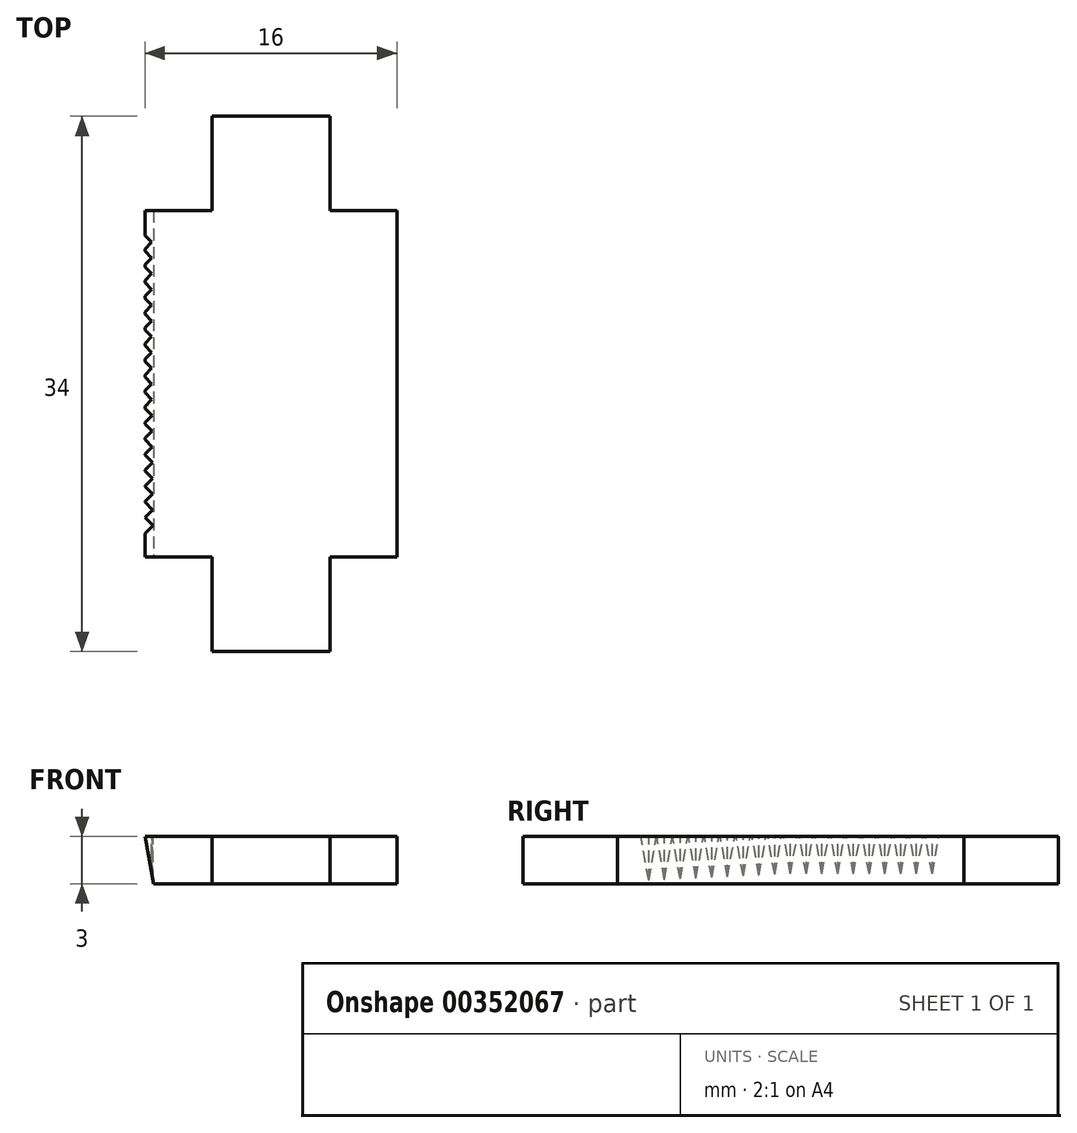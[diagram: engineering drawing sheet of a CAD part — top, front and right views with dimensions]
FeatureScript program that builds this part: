
annotation { "Feature Type Name" : "Feature", "Feature Type Description" : "" }
export const myFeature = defineFeature(function(context is Context, id is Id, definition is map)
    precondition{}
    {
        {
            var Q0;
            Q0=qCreatedBy(makeId("Front.planeOp"),FACE);
            var sketch = newSketch(context, id + "F0", { "sketchPlane" : qUnion([Q0])});
            skLineSegment(sketch, "E0.bottom", {"start": v(8, -1.5) * mm, "end": v(-8, -1.5) * mm});
            skLineSegment(sketch, "E0.top", {"start": v(8, 1.5) * mm, "end": v(-8, 1.5) * mm});
            skLineSegment(sketch, "E0.left", {"start": v(8, -1.5) * mm, "end": v(8, 1.5) * mm});
            skLineSegment(sketch, "E0.right", {"start": v(-8, -1.5) * mm, "end": v(-8, 1.5) * mm});
            skPoint(sketch, "E0.middle", {"position": v(0, 0) * mm});
            skSolve(sketch);
        }
        {
            var Q0;
            Q0=makeQuery(id+"F0.imprint","IMPRINT",FACE,{"disambiguationData":[TD([[makeQuery(id+"F0.imprint","IMPRINT",EDGE,{"derivedFrom":sQuery(id+"F0.wireOp",EDGE,"E0.bottom")}),-1.0]])]});
            extrude(context, id + "F1", {"entities" : qUnion([Q0]), "depth" : 22 * mm});
        }
        {
            var Q0;
            Q0=makeQuery(id+"F1.opExtrude","CAP_FACE",FACE,{"disambiguationData":[OSD([sQuery(id+"F0.wireOp",EDGE,"E0.bottom"),sQuery(id+"F0.wireOp",EDGE,"E0.top"),sQuery(id+"F0.wireOp",EDGE,"E0.left"),sQuery(id+"F0.wireOp",EDGE,"E0.right")])],"isStart":false});
            var sketch = newSketch(context, id + "F2", { "sketchPlane" : qUnion([Q0])});
            skLineSegment(sketch, "E1.bottom", {"start": v(3.75, -1.5) * mm, "end": v(-3.75, -1.5) * mm});
            skLineSegment(sketch, "E1.top", {"start": v(3.75, 1.5) * mm, "end": v(-3.75, 1.5) * mm});
            skLineSegment(sketch, "E1.left", {"start": v(3.75, -1.5) * mm, "end": v(3.75, 1.5) * mm});
            skLineSegment(sketch, "E1.right", {"start": v(-3.75, -1.5) * mm, "end": v(-3.75, 1.5) * mm});
            skPoint(sketch, "E1.middle", {"position": v(0, 0) * mm});
            skSolve(sketch);
        }
        {
            var Q0;
            Q0=makeQuery(id+"F2.imprint","IMPRINT",FACE,{"disambiguationData":[TD([[makeQuery(id+"F2.imprint","IMPRINT",EDGE,{"derivedFrom":sQuery(id+"F2.wireOp",EDGE,"E1.bottom")}),-1.0]])]});
            extrude(context, id + "F3", {"entities" : qUnion([Q0]), "operationType" : NewBodyOperationType.ADD, "depth" : 6 * mm});
        }
        {
            var Q0;
            Q0=makeQuery(id+"F1.opExtrude","CAP_FACE",FACE,{"disambiguationData":[OSD([sQuery(id+"F0.wireOp",EDGE,"E0.bottom"),sQuery(id+"F0.wireOp",EDGE,"E0.top"),sQuery(id+"F0.wireOp",EDGE,"E0.left"),sQuery(id+"F0.wireOp",EDGE,"E0.right")])],"isStart":true});
            var sketch = newSketch(context, id + "F4", { "sketchPlane" : qUnion([Q0])});
            skLineSegment(sketch, "E2.bottom", {"start": v(-3.75, -1.5) * mm, "end": v(3.75, -1.5) * mm});
            skLineSegment(sketch, "E2.top", {"start": v(-3.75, 1.5) * mm, "end": v(3.75, 1.5) * mm});
            skLineSegment(sketch, "E2.left", {"start": v(-3.75, -1.5) * mm, "end": v(-3.75, 1.5) * mm});
            skLineSegment(sketch, "E2.right", {"start": v(3.75, -1.5) * mm, "end": v(3.75, 1.5) * mm});
            skPoint(sketch, "E2.middle", {"position": v(0, 0) * mm});
            skSolve(sketch);
        }
        {
            var Q0;
            Q0=makeQuery(id+"F4.imprint","IMPRINT",FACE,{"disambiguationData":[TD([[makeQuery(id+"F4.imprint","IMPRINT",EDGE,{"derivedFrom":sQuery(id+"F4.wireOp",EDGE,"E2.bottom")}),1.0]])]});
            extrude(context, id + "F5", {"entities" : qUnion([Q0]), "operationType" : NewBodyOperationType.ADD, "depth" : 6 * mm});
        }
        {
            var Q0;
            Q0=makeQuery(id+"F5.boolean.opBoolean","MERGE",FACE,{"derivedFrom":[makeQuery(id+"F3.boolean.opBoolean","MERGE",FACE,{"derivedFrom":[makeQuery(id+"F1.opExtrude","SWEPT_FACE",FACE,{"disambiguationData":[OSD([sQuery(id+"F0.wireOp",EDGE,"E0.top")])]}),makeQuery(id+"F3.opExtrude","SWEPT_FACE",FACE,{"disambiguationData":[OSD([sQuery(id+"F2.wireOp",EDGE,"E1.top")])]})]}),makeQuery(id+"F5.opExtrude","SWEPT_FACE",FACE,{"disambiguationData":[OSD([sQuery(id+"F4.wireOp",EDGE,"E2.top")])]})]});
            var sketch = newSketch(context, id + "F6", { "sketchPlane" : qUnion([Q0])});
            skLineSegment(sketch, "E3", {"start": v(-8, -11) * mm, "end": v(8, -11) * mm, "construction": true});
            skLineSegment(sketch, "E4", {"start": v(-7.5, -11) * mm, "end": v(-8, -10.5) * mm});
            skLineSegment(sketch, "E5", {"start": v(-7.5, -11) * mm, "end": v(-8, -11.5) * mm});
            skPoint(sketch, "E6.orphan", {"position": v(-8.5, -10) * mm});
            skPoint(sketch, "E7.0.1.0", {"position": v(-8.5, -11) * mm});
            skLineSegment(sketch, "E7.0.1.1", {"start": v(-7.5, -12) * mm, "end": v(-8, -12.5) * mm});
            skLineSegment(sketch, "E7.0.1.2", {"start": v(-7.5, -12) * mm, "end": v(-8, -11.5) * mm});
            skPoint(sketch, "E7.0.2.0", {"position": v(-8.5, -12) * mm});
            skLineSegment(sketch, "E7.0.2.1", {"start": v(-7.5, -13) * mm, "end": v(-8, -13.5) * mm});
            skLineSegment(sketch, "E7.0.2.2", {"start": v(-7.5, -13) * mm, "end": v(-8, -12.5) * mm});
            skPoint(sketch, "E7.0.3.0", {"position": v(-8.5, -13) * mm});
            skLineSegment(sketch, "E7.0.3.1", {"start": v(-7.5, -14) * mm, "end": v(-8, -14.5) * mm});
            skLineSegment(sketch, "E7.0.3.2", {"start": v(-7.5, -14) * mm, "end": v(-8, -13.5) * mm});
            skPoint(sketch, "E7.0.4.0", {"position": v(-8.5, -14) * mm});
            skLineSegment(sketch, "E7.0.4.1", {"start": v(-7.5, -15) * mm, "end": v(-8, -15.5) * mm});
            skLineSegment(sketch, "E7.0.4.2", {"start": v(-7.5, -15) * mm, "end": v(-8, -14.5) * mm});
            skPoint(sketch, "E7.0.5.0", {"position": v(-8.5, -15) * mm});
            skLineSegment(sketch, "E7.0.5.1", {"start": v(-7.5, -16) * mm, "end": v(-8, -16.5) * mm});
            skLineSegment(sketch, "E7.0.5.2", {"start": v(-7.5, -16) * mm, "end": v(-8, -15.5) * mm});
            skPoint(sketch, "E7.0.6.0", {"position": v(-8.5, -16) * mm});
            skLineSegment(sketch, "E7.0.6.1", {"start": v(-7.5, -17) * mm, "end": v(-8, -17.5) * mm});
            skLineSegment(sketch, "E7.0.6.2", {"start": v(-7.5, -17) * mm, "end": v(-8, -16.5) * mm});
            skPoint(sketch, "E7.0.7.0", {"position": v(-8.5, -17) * mm});
            skLineSegment(sketch, "E7.0.7.1", {"start": v(-7.5, -18) * mm, "end": v(-8, -18.5) * mm});
            skLineSegment(sketch, "E7.0.7.2", {"start": v(-7.5, -18) * mm, "end": v(-8, -17.5) * mm});
            skPoint(sketch, "E7.0.8.0", {"position": v(-8.5, -18) * mm});
            skLineSegment(sketch, "E7.0.8.1", {"start": v(-7.5, -19) * mm, "end": v(-8, -19.5) * mm});
            skLineSegment(sketch, "E7.0.8.2", {"start": v(-7.5, -19) * mm, "end": v(-8, -18.5) * mm});
            skPoint(sketch, "E7.0.9.0", {"position": v(-8.5, -19) * mm});
            skLineSegment(sketch, "E7.0.9.1", {"start": v(-7.5, -20) * mm, "end": v(-8, -20.5) * mm});
            skLineSegment(sketch, "E7.0.9.2", {"start": v(-7.5, -20) * mm, "end": v(-8, -19.5) * mm});
            skPoint(sketch, "E7.1.0.0", {"position": v(-8.5, -9) * mm});
            skLineSegment(sketch, "E7.1.0.1", {"start": v(-7.5, -10) * mm, "end": v(-8, -10.5) * mm});
            skLineSegment(sketch, "E7.1.0.2", {"start": v(-7.5, -10) * mm, "end": v(-8, -9.5) * mm});
            skPoint(sketch, "E7.1.2.0", {"position": v(-8.5, -11) * mm});
            skLineSegment(sketch, "E7.1.2.1", {"start": v(-7.5, -12) * mm, "end": v(-8, -12.5) * mm});
            skLineSegment(sketch, "E7.1.2.2", {"start": v(-7.5, -12) * mm, "end": v(-8, -11.5) * mm});
            skPoint(sketch, "E7.1.3.0", {"position": v(-8.5, -12) * mm});
            skLineSegment(sketch, "E7.1.3.1", {"start": v(-7.5, -13) * mm, "end": v(-8, -13.5) * mm});
            skLineSegment(sketch, "E7.1.3.2", {"start": v(-7.5, -13) * mm, "end": v(-8, -12.5) * mm});
            skPoint(sketch, "E7.1.4.0", {"position": v(-8.5, -13) * mm});
            skLineSegment(sketch, "E7.1.4.1", {"start": v(-7.5, -14) * mm, "end": v(-8, -14.5) * mm});
            skLineSegment(sketch, "E7.1.4.2", {"start": v(-7.5, -14) * mm, "end": v(-8, -13.5) * mm});
            skPoint(sketch, "E7.1.5.0", {"position": v(-8.5, -14) * mm});
            skLineSegment(sketch, "E7.1.5.1", {"start": v(-7.5, -15) * mm, "end": v(-8, -15.5) * mm});
            skLineSegment(sketch, "E7.1.5.2", {"start": v(-7.5, -15) * mm, "end": v(-8, -14.5) * mm});
            skPoint(sketch, "E7.1.6.0", {"position": v(-8.5, -15) * mm});
            skLineSegment(sketch, "E7.1.6.1", {"start": v(-7.5, -16) * mm, "end": v(-8, -16.5) * mm});
            skLineSegment(sketch, "E7.1.6.2", {"start": v(-7.5, -16) * mm, "end": v(-8, -15.5) * mm});
            skPoint(sketch, "E7.1.7.0", {"position": v(-8.5, -16) * mm});
            skLineSegment(sketch, "E7.1.7.1", {"start": v(-7.5, -17) * mm, "end": v(-8, -17.5) * mm});
            skLineSegment(sketch, "E7.1.7.2", {"start": v(-7.5, -17) * mm, "end": v(-8, -16.5) * mm});
            skPoint(sketch, "E7.1.8.0", {"position": v(-8.5, -17) * mm});
            skLineSegment(sketch, "E7.1.8.1", {"start": v(-7.5, -18) * mm, "end": v(-8, -18.5) * mm});
            skLineSegment(sketch, "E7.1.8.2", {"start": v(-7.5, -18) * mm, "end": v(-8, -17.5) * mm});
            skPoint(sketch, "E7.1.9.0", {"position": v(-8.5, -18) * mm});
            skLineSegment(sketch, "E7.1.9.1", {"start": v(-7.5, -19) * mm, "end": v(-8, -19.5) * mm});
            skLineSegment(sketch, "E7.1.9.2", {"start": v(-7.5, -19) * mm, "end": v(-8, -18.5) * mm});
            skPoint(sketch, "E7.2.0.0", {"position": v(-8.52, -8) * mm});
            skLineSegment(sketch, "E7.2.0.1", {"start": v(-7.52, -9) * mm, "end": v(-8.02, -9.5) * mm});
            skLineSegment(sketch, "E7.2.0.2", {"start": v(-7.52, -9) * mm, "end": v(-8.02, -8.5) * mm});
            skPoint(sketch, "E7.2.1.0", {"position": v(-8.52, -9) * mm});
            skLineSegment(sketch, "E7.2.1.1", {"start": v(-7.52, -10) * mm, "end": v(-8.02, -10.5) * mm});
            skLineSegment(sketch, "E7.2.1.2", {"start": v(-7.52, -10) * mm, "end": v(-8.02, -9.5) * mm});
            skPoint(sketch, "E7.2.2.0", {"position": v(-8.52, -10) * mm});
            skLineSegment(sketch, "E7.2.2.1", {"start": v(-7.52, -11) * mm, "end": v(-8.02, -11.5) * mm});
            skLineSegment(sketch, "E7.2.2.2", {"start": v(-7.52, -11) * mm, "end": v(-8.02, -10.5) * mm});
            skPoint(sketch, "E7.2.3.0", {"position": v(-8.52, -11) * mm});
            skLineSegment(sketch, "E7.2.3.1", {"start": v(-7.52, -12) * mm, "end": v(-8.02, -12.5) * mm});
            skLineSegment(sketch, "E7.2.3.2", {"start": v(-7.52, -12) * mm, "end": v(-8.02, -11.5) * mm});
            skPoint(sketch, "E7.2.4.0", {"position": v(-8.52, -12) * mm});
            skLineSegment(sketch, "E7.2.4.1", {"start": v(-7.52, -13) * mm, "end": v(-8.02, -13.5) * mm});
            skLineSegment(sketch, "E7.2.4.2", {"start": v(-7.52, -13) * mm, "end": v(-8.02, -12.5) * mm});
            skPoint(sketch, "E7.2.5.0", {"position": v(-8.52, -13) * mm});
            skLineSegment(sketch, "E7.2.5.1", {"start": v(-7.52, -14) * mm, "end": v(-8.02, -14.5) * mm});
            skLineSegment(sketch, "E7.2.5.2", {"start": v(-7.52, -14) * mm, "end": v(-8.02, -13.5) * mm});
            skPoint(sketch, "E7.2.6.0", {"position": v(-8.52, -14) * mm});
            skLineSegment(sketch, "E7.2.6.1", {"start": v(-7.52, -15) * mm, "end": v(-8.02, -15.5) * mm});
            skLineSegment(sketch, "E7.2.6.2", {"start": v(-7.52, -15) * mm, "end": v(-8.02, -14.5) * mm});
            skPoint(sketch, "E7.2.7.0", {"position": v(-8.52, -15) * mm});
            skLineSegment(sketch, "E7.2.7.1", {"start": v(-7.52, -16) * mm, "end": v(-8.02, -16.5) * mm});
            skLineSegment(sketch, "E7.2.7.2", {"start": v(-7.52, -16) * mm, "end": v(-8.02, -15.5) * mm});
            skPoint(sketch, "E7.2.8.0", {"position": v(-8.52, -16) * mm});
            skLineSegment(sketch, "E7.2.8.1", {"start": v(-7.52, -17) * mm, "end": v(-8.02, -17.5) * mm});
            skLineSegment(sketch, "E7.2.8.2", {"start": v(-7.52, -17) * mm, "end": v(-8.02, -16.5) * mm});
            skPoint(sketch, "E7.2.9.0", {"position": v(-8.52, -17) * mm});
            skLineSegment(sketch, "E7.2.9.1", {"start": v(-7.52, -18) * mm, "end": v(-8.02, -18.5) * mm});
            skLineSegment(sketch, "E7.2.9.2", {"start": v(-7.52, -18) * mm, "end": v(-8.02, -17.5) * mm});
            skPoint(sketch, "E7.3.0.0", {"position": v(-8.52, -7) * mm});
            skLineSegment(sketch, "E7.3.0.1", {"start": v(-7.52, -8) * mm, "end": v(-8.02, -8.5) * mm});
            skLineSegment(sketch, "E7.3.0.2", {"start": v(-7.52, -8) * mm, "end": v(-8.02, -7.5) * mm});
            skPoint(sketch, "E7.3.1.0", {"position": v(-8.52, -8) * mm});
            skLineSegment(sketch, "E7.3.1.1", {"start": v(-7.52, -9) * mm, "end": v(-8.02, -9.5) * mm});
            skLineSegment(sketch, "E7.3.1.2", {"start": v(-7.52, -9) * mm, "end": v(-8.02, -8.5) * mm});
            skPoint(sketch, "E7.3.2.0", {"position": v(-8.52, -9) * mm});
            skLineSegment(sketch, "E7.3.2.1", {"start": v(-7.52, -10) * mm, "end": v(-8.02, -10.5) * mm});
            skLineSegment(sketch, "E7.3.2.2", {"start": v(-7.52, -10) * mm, "end": v(-8.02, -9.5) * mm});
            skPoint(sketch, "E7.3.3.0", {"position": v(-8.52, -10) * mm});
            skLineSegment(sketch, "E7.3.3.1", {"start": v(-7.52, -11) * mm, "end": v(-8.02, -11.5) * mm});
            skLineSegment(sketch, "E7.3.3.2", {"start": v(-7.52, -11) * mm, "end": v(-8.02, -10.5) * mm});
            skPoint(sketch, "E7.3.4.0", {"position": v(-8.52, -11) * mm});
            skLineSegment(sketch, "E7.3.4.1", {"start": v(-7.52, -12) * mm, "end": v(-8.02, -12.5) * mm});
            skLineSegment(sketch, "E7.3.4.2", {"start": v(-7.52, -12) * mm, "end": v(-8.02, -11.5) * mm});
            skPoint(sketch, "E7.3.5.0", {"position": v(-8.52, -12) * mm});
            skLineSegment(sketch, "E7.3.5.1", {"start": v(-7.52, -13) * mm, "end": v(-8.02, -13.5) * mm});
            skLineSegment(sketch, "E7.3.5.2", {"start": v(-7.52, -13) * mm, "end": v(-8.02, -12.5) * mm});
            skPoint(sketch, "E7.3.6.0", {"position": v(-8.52, -13) * mm});
            skLineSegment(sketch, "E7.3.6.1", {"start": v(-7.52, -14) * mm, "end": v(-8.02, -14.5) * mm});
            skLineSegment(sketch, "E7.3.6.2", {"start": v(-7.52, -14) * mm, "end": v(-8.02, -13.5) * mm});
            skPoint(sketch, "E7.3.7.0", {"position": v(-8.52, -14) * mm});
            skLineSegment(sketch, "E7.3.7.1", {"start": v(-7.52, -15) * mm, "end": v(-8.02, -15.5) * mm});
            skLineSegment(sketch, "E7.3.7.2", {"start": v(-7.52, -15) * mm, "end": v(-8.02, -14.5) * mm});
            skPoint(sketch, "E7.3.8.0", {"position": v(-8.52, -15) * mm});
            skLineSegment(sketch, "E7.3.8.1", {"start": v(-7.52, -16) * mm, "end": v(-8.02, -16.5) * mm});
            skLineSegment(sketch, "E7.3.8.2", {"start": v(-7.52, -16) * mm, "end": v(-8.02, -15.5) * mm});
            skPoint(sketch, "E7.3.9.0", {"position": v(-8.52, -16) * mm});
            skLineSegment(sketch, "E7.3.9.1", {"start": v(-7.52, -17) * mm, "end": v(-8.02, -17.5) * mm});
            skLineSegment(sketch, "E7.3.9.2", {"start": v(-7.52, -17) * mm, "end": v(-8.02, -16.5) * mm});
            skPoint(sketch, "E7.4.0.0", {"position": v(-8.53, -6) * mm});
            skLineSegment(sketch, "E7.4.0.1", {"start": v(-7.53, -7) * mm, "end": v(-8.03, -7.5) * mm});
            skLineSegment(sketch, "E7.4.0.2", {"start": v(-7.53, -7) * mm, "end": v(-8.03, -6.5) * mm});
            skPoint(sketch, "E7.4.1.0", {"position": v(-8.53, -7) * mm});
            skLineSegment(sketch, "E7.4.1.1", {"start": v(-7.53, -8) * mm, "end": v(-8.03, -8.5) * mm});
            skLineSegment(sketch, "E7.4.1.2", {"start": v(-7.53, -8) * mm, "end": v(-8.03, -7.5) * mm});
            skPoint(sketch, "E7.4.2.0", {"position": v(-8.53, -8) * mm});
            skLineSegment(sketch, "E7.4.2.1", {"start": v(-7.53, -9) * mm, "end": v(-8.03, -9.5) * mm});
            skLineSegment(sketch, "E7.4.2.2", {"start": v(-7.53, -9) * mm, "end": v(-8.03, -8.5) * mm});
            skPoint(sketch, "E7.4.3.0", {"position": v(-8.53, -9) * mm});
            skLineSegment(sketch, "E7.4.3.1", {"start": v(-7.53, -10) * mm, "end": v(-8.03, -10.5) * mm});
            skLineSegment(sketch, "E7.4.3.2", {"start": v(-7.53, -10) * mm, "end": v(-8.03, -9.5) * mm});
            skPoint(sketch, "E7.4.4.0", {"position": v(-8.53, -10) * mm});
            skLineSegment(sketch, "E7.4.4.1", {"start": v(-7.53, -11) * mm, "end": v(-8.03, -11.5) * mm});
            skLineSegment(sketch, "E7.4.4.2", {"start": v(-7.53, -11) * mm, "end": v(-8.03, -10.5) * mm});
            skPoint(sketch, "E7.4.5.0", {"position": v(-8.53, -11) * mm});
            skLineSegment(sketch, "E7.4.5.1", {"start": v(-7.53, -12) * mm, "end": v(-8.03, -12.5) * mm});
            skLineSegment(sketch, "E7.4.5.2", {"start": v(-7.53, -12) * mm, "end": v(-8.03, -11.5) * mm});
            skPoint(sketch, "E7.4.6.0", {"position": v(-8.53, -12) * mm});
            skLineSegment(sketch, "E7.4.6.1", {"start": v(-7.53, -13) * mm, "end": v(-8.03, -13.5) * mm});
            skLineSegment(sketch, "E7.4.6.2", {"start": v(-7.53, -13) * mm, "end": v(-8.03, -12.5) * mm});
            skPoint(sketch, "E7.4.7.0", {"position": v(-8.53, -13) * mm});
            skLineSegment(sketch, "E7.4.7.1", {"start": v(-7.53, -14) * mm, "end": v(-8.03, -14.5) * mm});
            skLineSegment(sketch, "E7.4.7.2", {"start": v(-7.53, -14) * mm, "end": v(-8.03, -13.5) * mm});
            skPoint(sketch, "E7.4.8.0", {"position": v(-8.53, -14) * mm});
            skLineSegment(sketch, "E7.4.8.1", {"start": v(-7.53, -15) * mm, "end": v(-8.03, -15.5) * mm});
            skLineSegment(sketch, "E7.4.8.2", {"start": v(-7.53, -15) * mm, "end": v(-8.03, -14.5) * mm});
            skPoint(sketch, "E7.4.9.0", {"position": v(-8.53, -15) * mm});
            skLineSegment(sketch, "E7.4.9.1", {"start": v(-7.53, -16) * mm, "end": v(-8.03, -16.5) * mm});
            skLineSegment(sketch, "E7.4.9.2", {"start": v(-7.53, -16) * mm, "end": v(-8.03, -15.5) * mm});
            skPoint(sketch, "E7.5.0.0", {"position": v(-8.54, -5) * mm});
            skLineSegment(sketch, "E7.5.0.1", {"start": v(-7.54, -6) * mm, "end": v(-8.04, -6.5) * mm});
            skLineSegment(sketch, "E7.5.0.2", {"start": v(-7.54, -6) * mm, "end": v(-8.04, -5.5) * mm});
            skPoint(sketch, "E7.5.1.0", {"position": v(-8.54, -6) * mm});
            skLineSegment(sketch, "E7.5.1.1", {"start": v(-7.54, -7) * mm, "end": v(-8.04, -7.5) * mm});
            skLineSegment(sketch, "E7.5.1.2", {"start": v(-7.54, -7) * mm, "end": v(-8.04, -6.5) * mm});
            skPoint(sketch, "E7.5.2.0", {"position": v(-8.54, -7) * mm});
            skLineSegment(sketch, "E7.5.2.1", {"start": v(-7.54, -8) * mm, "end": v(-8.04, -8.5) * mm});
            skLineSegment(sketch, "E7.5.2.2", {"start": v(-7.54, -8) * mm, "end": v(-8.04, -7.5) * mm});
            skPoint(sketch, "E7.5.3.0", {"position": v(-8.54, -8) * mm});
            skLineSegment(sketch, "E7.5.3.1", {"start": v(-7.54, -9) * mm, "end": v(-8.04, -9.5) * mm});
            skLineSegment(sketch, "E7.5.3.2", {"start": v(-7.54, -9) * mm, "end": v(-8.04, -8.5) * mm});
            skPoint(sketch, "E7.5.4.0", {"position": v(-8.54, -9) * mm});
            skLineSegment(sketch, "E7.5.4.1", {"start": v(-7.54, -10) * mm, "end": v(-8.04, -10.5) * mm});
            skLineSegment(sketch, "E7.5.4.2", {"start": v(-7.54, -10) * mm, "end": v(-8.04, -9.5) * mm});
            skPoint(sketch, "E7.5.5.0", {"position": v(-8.54, -10) * mm});
            skLineSegment(sketch, "E7.5.5.1", {"start": v(-7.54, -11) * mm, "end": v(-8.04, -11.5) * mm});
            skLineSegment(sketch, "E7.5.5.2", {"start": v(-7.54, -11) * mm, "end": v(-8.04, -10.5) * mm});
            skPoint(sketch, "E7.5.6.0", {"position": v(-8.54, -11) * mm});
            skLineSegment(sketch, "E7.5.6.1", {"start": v(-7.54, -12) * mm, "end": v(-8.04, -12.5) * mm});
            skLineSegment(sketch, "E7.5.6.2", {"start": v(-7.54, -12) * mm, "end": v(-8.04, -11.5) * mm});
            skPoint(sketch, "E7.5.7.0", {"position": v(-8.54, -12) * mm});
            skLineSegment(sketch, "E7.5.7.1", {"start": v(-7.54, -13) * mm, "end": v(-8.04, -13.5) * mm});
            skLineSegment(sketch, "E7.5.7.2", {"start": v(-7.54, -13) * mm, "end": v(-8.04, -12.5) * mm});
            skPoint(sketch, "E7.5.8.0", {"position": v(-8.54, -13) * mm});
            skLineSegment(sketch, "E7.5.8.1", {"start": v(-7.54, -14) * mm, "end": v(-8.04, -14.5) * mm});
            skLineSegment(sketch, "E7.5.8.2", {"start": v(-7.54, -14) * mm, "end": v(-8.04, -13.5) * mm});
            skPoint(sketch, "E7.5.9.0", {"position": v(-8.54, -14) * mm});
            skLineSegment(sketch, "E7.5.9.1", {"start": v(-7.54, -15) * mm, "end": v(-8.04, -15.5) * mm});
            skLineSegment(sketch, "E7.5.9.2", {"start": v(-7.54, -15) * mm, "end": v(-8.04, -14.5) * mm});
            skPoint(sketch, "E7.6.0.0", {"position": v(-8.55, -4) * mm});
            skLineSegment(sketch, "E7.6.0.1", {"start": v(-7.55, -5) * mm, "end": v(-8.05, -5.5) * mm});
            skLineSegment(sketch, "E7.6.0.2", {"start": v(-7.55, -5) * mm, "end": v(-8.05, -4.5) * mm});
            skPoint(sketch, "E7.6.1.0", {"position": v(-8.55, -5) * mm});
            skLineSegment(sketch, "E7.6.1.1", {"start": v(-7.55, -6) * mm, "end": v(-8.05, -6.5) * mm});
            skLineSegment(sketch, "E7.6.1.2", {"start": v(-7.55, -6) * mm, "end": v(-8.05, -5.5) * mm});
            skPoint(sketch, "E7.6.2.0", {"position": v(-8.55, -6) * mm});
            skLineSegment(sketch, "E7.6.2.1", {"start": v(-7.55, -7) * mm, "end": v(-8.05, -7.5) * mm});
            skLineSegment(sketch, "E7.6.2.2", {"start": v(-7.55, -7) * mm, "end": v(-8.05, -6.5) * mm});
            skPoint(sketch, "E7.6.3.0", {"position": v(-8.55, -7) * mm});
            skLineSegment(sketch, "E7.6.3.1", {"start": v(-7.55, -8) * mm, "end": v(-8.05, -8.5) * mm});
            skLineSegment(sketch, "E7.6.3.2", {"start": v(-7.55, -8) * mm, "end": v(-8.05, -7.5) * mm});
            skPoint(sketch, "E7.6.4.0", {"position": v(-8.55, -8) * mm});
            skLineSegment(sketch, "E7.6.4.1", {"start": v(-7.55, -9) * mm, "end": v(-8.05, -9.5) * mm});
            skLineSegment(sketch, "E7.6.4.2", {"start": v(-7.55, -9) * mm, "end": v(-8.05, -8.5) * mm});
            skPoint(sketch, "E7.6.5.0", {"position": v(-8.55, -9) * mm});
            skLineSegment(sketch, "E7.6.5.1", {"start": v(-7.55, -10) * mm, "end": v(-8.05, -10.5) * mm});
            skLineSegment(sketch, "E7.6.5.2", {"start": v(-7.55, -10) * mm, "end": v(-8.05, -9.5) * mm});
            skPoint(sketch, "E7.6.6.0", {"position": v(-8.55, -10) * mm});
            skLineSegment(sketch, "E7.6.6.1", {"start": v(-7.55, -11) * mm, "end": v(-8.05, -11.5) * mm});
            skLineSegment(sketch, "E7.6.6.2", {"start": v(-7.55, -11) * mm, "end": v(-8.05, -10.5) * mm});
            skPoint(sketch, "E7.6.7.0", {"position": v(-8.55, -11) * mm});
            skLineSegment(sketch, "E7.6.7.1", {"start": v(-7.55, -12) * mm, "end": v(-8.05, -12.5) * mm});
            skLineSegment(sketch, "E7.6.7.2", {"start": v(-7.55, -12) * mm, "end": v(-8.05, -11.5) * mm});
            skPoint(sketch, "E7.6.8.0", {"position": v(-8.55, -12) * mm});
            skLineSegment(sketch, "E7.6.8.1", {"start": v(-7.55, -13) * mm, "end": v(-8.05, -13.5) * mm});
            skLineSegment(sketch, "E7.6.8.2", {"start": v(-7.55, -13) * mm, "end": v(-8.05, -12.5) * mm});
            skPoint(sketch, "E7.6.9.0", {"position": v(-8.55, -13) * mm});
            skLineSegment(sketch, "E7.6.9.1", {"start": v(-7.55, -14) * mm, "end": v(-8.05, -14.5) * mm});
            skLineSegment(sketch, "E7.6.9.2", {"start": v(-7.55, -14) * mm, "end": v(-8.05, -13.5) * mm});
            skPoint(sketch, "E7.7.0.0", {"position": v(-8.56, -3) * mm});
            skLineSegment(sketch, "E7.7.0.1", {"start": v(-7.56, -4) * mm, "end": v(-8.06, -4.5) * mm});
            skLineSegment(sketch, "E7.7.0.2", {"start": v(-7.56, -4) * mm, "end": v(-8.06, -3.5) * mm});
            skPoint(sketch, "E7.7.1.0", {"position": v(-8.56, -4) * mm});
            skLineSegment(sketch, "E7.7.1.1", {"start": v(-7.56, -5) * mm, "end": v(-8.06, -5.5) * mm});
            skLineSegment(sketch, "E7.7.1.2", {"start": v(-7.56, -5) * mm, "end": v(-8.06, -4.5) * mm});
            skPoint(sketch, "E7.7.2.0", {"position": v(-8.56, -5) * mm});
            skLineSegment(sketch, "E7.7.2.1", {"start": v(-7.56, -6) * mm, "end": v(-8.06, -6.5) * mm});
            skLineSegment(sketch, "E7.7.2.2", {"start": v(-7.56, -6) * mm, "end": v(-8.06, -5.5) * mm});
            skPoint(sketch, "E7.7.3.0", {"position": v(-8.56, -6) * mm});
            skLineSegment(sketch, "E7.7.3.1", {"start": v(-7.56, -7) * mm, "end": v(-8.06, -7.5) * mm});
            skLineSegment(sketch, "E7.7.3.2", {"start": v(-7.56, -7) * mm, "end": v(-8.06, -6.5) * mm});
            skPoint(sketch, "E7.7.4.0", {"position": v(-8.56, -7) * mm});
            skLineSegment(sketch, "E7.7.4.1", {"start": v(-7.56, -8) * mm, "end": v(-8.06, -8.5) * mm});
            skLineSegment(sketch, "E7.7.4.2", {"start": v(-7.56, -8) * mm, "end": v(-8.06, -7.5) * mm});
            skPoint(sketch, "E7.7.5.0", {"position": v(-8.56, -8) * mm});
            skLineSegment(sketch, "E7.7.5.1", {"start": v(-7.56, -9) * mm, "end": v(-8.06, -9.5) * mm});
            skLineSegment(sketch, "E7.7.5.2", {"start": v(-7.56, -9) * mm, "end": v(-8.06, -8.5) * mm});
            skPoint(sketch, "E7.7.6.0", {"position": v(-8.56, -9) * mm});
            skLineSegment(sketch, "E7.7.6.1", {"start": v(-7.56, -10) * mm, "end": v(-8.06, -10.5) * mm});
            skLineSegment(sketch, "E7.7.6.2", {"start": v(-7.56, -10) * mm, "end": v(-8.06, -9.5) * mm});
            skPoint(sketch, "E7.7.7.0", {"position": v(-8.56, -10) * mm});
            skLineSegment(sketch, "E7.7.7.1", {"start": v(-7.56, -11) * mm, "end": v(-8.06, -11.5) * mm});
            skLineSegment(sketch, "E7.7.7.2", {"start": v(-7.56, -11) * mm, "end": v(-8.06, -10.5) * mm});
            skPoint(sketch, "E7.7.8.0", {"position": v(-8.56, -11) * mm});
            skLineSegment(sketch, "E7.7.8.1", {"start": v(-7.56, -12) * mm, "end": v(-8.06, -12.5) * mm});
            skLineSegment(sketch, "E7.7.8.2", {"start": v(-7.56, -12) * mm, "end": v(-8.06, -11.5) * mm});
            skPoint(sketch, "E7.7.9.0", {"position": v(-8.56, -12) * mm});
            skLineSegment(sketch, "E7.7.9.1", {"start": v(-7.56, -13) * mm, "end": v(-8.06, -13.5) * mm});
            skLineSegment(sketch, "E7.7.9.2", {"start": v(-7.56, -13) * mm, "end": v(-8.06, -12.5) * mm});
            skPoint(sketch, "E7.8.0.0", {"position": v(-8.57, -2) * mm});
            skLineSegment(sketch, "E7.8.0.1", {"start": v(-7.57, -3) * mm, "end": v(-8.07, -3.5) * mm});
            skLineSegment(sketch, "E7.8.0.2", {"start": v(-7.57, -3) * mm, "end": v(-8.07, -2.5) * mm});
            skPoint(sketch, "E7.8.1.0", {"position": v(-8.57, -3) * mm});
            skLineSegment(sketch, "E7.8.1.1", {"start": v(-7.57, -4) * mm, "end": v(-8.07, -4.5) * mm});
            skLineSegment(sketch, "E7.8.1.2", {"start": v(-7.57, -4) * mm, "end": v(-8.07, -3.5) * mm});
            skPoint(sketch, "E7.8.2.0", {"position": v(-8.57, -4) * mm});
            skLineSegment(sketch, "E7.8.2.1", {"start": v(-7.57, -5) * mm, "end": v(-8.07, -5.5) * mm});
            skLineSegment(sketch, "E7.8.2.2", {"start": v(-7.57, -5) * mm, "end": v(-8.07, -4.5) * mm});
            skPoint(sketch, "E7.8.3.0", {"position": v(-8.57, -5) * mm});
            skLineSegment(sketch, "E7.8.3.1", {"start": v(-7.57, -6) * mm, "end": v(-8.07, -6.5) * mm});
            skLineSegment(sketch, "E7.8.3.2", {"start": v(-7.57, -6) * mm, "end": v(-8.07, -5.5) * mm});
            skPoint(sketch, "E7.8.4.0", {"position": v(-8.57, -6) * mm});
            skLineSegment(sketch, "E7.8.4.1", {"start": v(-7.57, -7) * mm, "end": v(-8.07, -7.5) * mm});
            skLineSegment(sketch, "E7.8.4.2", {"start": v(-7.57, -7) * mm, "end": v(-8.07, -6.5) * mm});
            skPoint(sketch, "E7.8.5.0", {"position": v(-8.57, -7) * mm});
            skLineSegment(sketch, "E7.8.5.1", {"start": v(-7.57, -8) * mm, "end": v(-8.07, -8.5) * mm});
            skLineSegment(sketch, "E7.8.5.2", {"start": v(-7.57, -8) * mm, "end": v(-8.07, -7.5) * mm});
            skPoint(sketch, "E7.8.6.0", {"position": v(-8.57, -8) * mm});
            skLineSegment(sketch, "E7.8.6.1", {"start": v(-7.57, -9) * mm, "end": v(-8.07, -9.5) * mm});
            skLineSegment(sketch, "E7.8.6.2", {"start": v(-7.57, -9) * mm, "end": v(-8.07, -8.5) * mm});
            skPoint(sketch, "E7.8.7.0", {"position": v(-8.57, -9) * mm});
            skLineSegment(sketch, "E7.8.7.1", {"start": v(-7.57, -10) * mm, "end": v(-8.07, -10.5) * mm});
            skLineSegment(sketch, "E7.8.7.2", {"start": v(-7.57, -10) * mm, "end": v(-8.07, -9.5) * mm});
            skPoint(sketch, "E7.8.8.0", {"position": v(-8.57, -10) * mm});
            skLineSegment(sketch, "E7.8.8.1", {"start": v(-7.57, -11) * mm, "end": v(-8.07, -11.5) * mm});
            skLineSegment(sketch, "E7.8.8.2", {"start": v(-7.57, -11) * mm, "end": v(-8.07, -10.5) * mm});
            skPoint(sketch, "E7.8.9.0", {"position": v(-8.57, -11) * mm});
            skLineSegment(sketch, "E7.8.9.1", {"start": v(-7.57, -12) * mm, "end": v(-8.07, -12.5) * mm});
            skLineSegment(sketch, "E7.8.9.2", {"start": v(-7.57, -12) * mm, "end": v(-8.07, -11.5) * mm});
            skPoint(sketch, "E7.9.0.0", {"position": v(-8.57, -1) * mm});
            skLineSegment(sketch, "E7.9.0.1", {"start": v(-7.57, -2) * mm, "end": v(-8.07, -2.5) * mm});
            skLineSegment(sketch, "E7.9.0.2", {"start": v(-7.57, -2) * mm, "end": v(-8.07, -1.5) * mm});
            skPoint(sketch, "E7.9.1.0", {"position": v(-8.57, -2) * mm});
            skLineSegment(sketch, "E7.9.1.1", {"start": v(-7.57, -3) * mm, "end": v(-8.07, -3.5) * mm});
            skLineSegment(sketch, "E7.9.1.2", {"start": v(-7.57, -3) * mm, "end": v(-8.07, -2.5) * mm});
            skPoint(sketch, "E7.9.2.0", {"position": v(-8.57, -3) * mm});
            skLineSegment(sketch, "E7.9.2.1", {"start": v(-7.57, -4) * mm, "end": v(-8.07, -4.5) * mm});
            skLineSegment(sketch, "E7.9.2.2", {"start": v(-7.57, -4) * mm, "end": v(-8.07, -3.5) * mm});
            skPoint(sketch, "E7.9.3.0", {"position": v(-8.57, -4) * mm});
            skLineSegment(sketch, "E7.9.3.1", {"start": v(-7.57, -5) * mm, "end": v(-8.07, -5.5) * mm});
            skLineSegment(sketch, "E7.9.3.2", {"start": v(-7.57, -5) * mm, "end": v(-8.07, -4.5) * mm});
            skPoint(sketch, "E7.9.4.0", {"position": v(-8.57, -5) * mm});
            skLineSegment(sketch, "E7.9.4.1", {"start": v(-7.57, -6) * mm, "end": v(-8.07, -6.5) * mm});
            skLineSegment(sketch, "E7.9.4.2", {"start": v(-7.57, -6) * mm, "end": v(-8.07, -5.5) * mm});
            skPoint(sketch, "E7.9.5.0", {"position": v(-8.57, -6) * mm});
            skLineSegment(sketch, "E7.9.5.1", {"start": v(-7.57, -7) * mm, "end": v(-8.07, -7.5) * mm});
            skLineSegment(sketch, "E7.9.5.2", {"start": v(-7.57, -7) * mm, "end": v(-8.07, -6.5) * mm});
            skPoint(sketch, "E7.9.6.0", {"position": v(-8.57, -7) * mm});
            skLineSegment(sketch, "E7.9.6.1", {"start": v(-7.57, -8) * mm, "end": v(-8.07, -8.5) * mm});
            skLineSegment(sketch, "E7.9.6.2", {"start": v(-7.57, -8) * mm, "end": v(-8.07, -7.5) * mm});
            skPoint(sketch, "E7.9.7.0", {"position": v(-8.57, -8) * mm});
            skLineSegment(sketch, "E7.9.7.1", {"start": v(-7.57, -9) * mm, "end": v(-8.07, -9.5) * mm});
            skLineSegment(sketch, "E7.9.7.2", {"start": v(-7.57, -9) * mm, "end": v(-8.07, -8.5) * mm});
            skPoint(sketch, "E7.9.8.0", {"position": v(-8.57, -9) * mm});
            skLineSegment(sketch, "E7.9.8.1", {"start": v(-7.57, -10) * mm, "end": v(-8.07, -10.5) * mm});
            skLineSegment(sketch, "E7.9.8.2", {"start": v(-7.57, -10) * mm, "end": v(-8.07, -9.5) * mm});
            skPoint(sketch, "E7.9.9.0", {"position": v(-8.57, -10) * mm});
            skLineSegment(sketch, "E7.9.9.1", {"start": v(-7.57, -11) * mm, "end": v(-8.07, -11.5) * mm});
            skLineSegment(sketch, "E7.9.9.2", {"start": v(-7.57, -11) * mm, "end": v(-8.07, -10.5) * mm});
            skLineSegment(sketch, "E7.direction1", {"start": v(-8, -11.5) * mm, "end": v(-8, -10.5) * mm, "construction": true});
            skLineSegment(sketch, "E7.direction2", {"start": v(-8, -11.5) * mm, "end": v(-8, -12.5) * mm, "construction": true});
            skSolve(sketch);
        }
        {
            var Q0;
            Q0=qSketchRegion(id+"F6",true);
            var Q1;
            {var subQ0=sQuery(id+"F6.wireOp",EDGE,"E7.9.0.2");var subQ1=sQuery(id+"F6.wireOp",EDGE,"E7.9.0.1");var subQ2=makeQuery(id+"F6.imprint","INTERSECT",VERTEX,{"derivedFrom":[subQ1,subQ0]});Q1=makeQuery(id+"F6.imprint","IMPRINT",FACE,{"disambiguationData":[TD([[makeQuery(id+"F6.imprint","IMPRINT",EDGE,{"disambiguationData":[TD([[subQ2,-1.0]])],"derivedFrom":subQ1}),-1.0]])]});}
            var Q2;
            {var subQ0=sQuery(id+"F6.wireOp",EDGE,"E7.9.1.2");var subQ1=sQuery(id+"F6.wireOp",EDGE,"E7.9.1.1");var subQ2=makeQuery(id+"F6.imprint","INTERSECT",VERTEX,{"derivedFrom":[subQ1,subQ0]});Q2=makeQuery(id+"F6.imprint","IMPRINT",FACE,{"disambiguationData":[TD([[makeQuery(id+"F6.imprint","IMPRINT",EDGE,{"disambiguationData":[TD([[subQ2,-1.0]])],"derivedFrom":subQ1}),-1.0]])]});}
            var Q3;
            {var subQ0=sQuery(id+"F6.wireOp",EDGE,"E7.9.2.2");var subQ1=sQuery(id+"F6.wireOp",EDGE,"E7.9.2.1");var subQ2=makeQuery(id+"F6.imprint","INTERSECT",VERTEX,{"derivedFrom":[subQ1,subQ0]});Q3=makeQuery(id+"F6.imprint","IMPRINT",FACE,{"disambiguationData":[TD([[makeQuery(id+"F6.imprint","IMPRINT",EDGE,{"disambiguationData":[TD([[subQ2,-1.0]])],"derivedFrom":subQ1}),-1.0]])]});}
            var Q4;
            {var subQ0=sQuery(id+"F6.wireOp",EDGE,"E7.9.3.2");var subQ1=sQuery(id+"F6.wireOp",EDGE,"E7.9.3.1");var subQ2=makeQuery(id+"F6.imprint","INTERSECT",VERTEX,{"derivedFrom":[subQ1,subQ0]});Q4=makeQuery(id+"F6.imprint","IMPRINT",FACE,{"disambiguationData":[TD([[makeQuery(id+"F6.imprint","IMPRINT",EDGE,{"disambiguationData":[TD([[subQ2,-1.0]])],"derivedFrom":subQ1}),-1.0]])]});}
            var Q5;
            {var subQ0=sQuery(id+"F6.wireOp",EDGE,"E7.9.4.2");var subQ1=sQuery(id+"F6.wireOp",EDGE,"E7.9.4.1");var subQ2=makeQuery(id+"F6.imprint","INTERSECT",VERTEX,{"derivedFrom":[subQ1,subQ0]});Q5=makeQuery(id+"F6.imprint","IMPRINT",FACE,{"disambiguationData":[TD([[makeQuery(id+"F6.imprint","IMPRINT",EDGE,{"disambiguationData":[TD([[subQ2,-1.0]])],"derivedFrom":subQ1}),-1.0]])]});}
            var Q6;
            {var subQ0=sQuery(id+"F6.wireOp",EDGE,"E7.9.5.2");var subQ1=sQuery(id+"F6.wireOp",EDGE,"E7.9.5.1");var subQ2=makeQuery(id+"F6.imprint","INTERSECT",VERTEX,{"derivedFrom":[subQ1,subQ0]});Q6=makeQuery(id+"F6.imprint","IMPRINT",FACE,{"disambiguationData":[TD([[makeQuery(id+"F6.imprint","IMPRINT",EDGE,{"disambiguationData":[TD([[subQ2,-1.0]])],"derivedFrom":subQ1}),-1.0]])]});}
            var Q7;
            {var subQ0=sQuery(id+"F6.wireOp",EDGE,"E7.9.6.2");var subQ1=sQuery(id+"F6.wireOp",EDGE,"E7.9.6.1");var subQ2=makeQuery(id+"F6.imprint","INTERSECT",VERTEX,{"derivedFrom":[subQ1,subQ0]});Q7=makeQuery(id+"F6.imprint","IMPRINT",FACE,{"disambiguationData":[TD([[makeQuery(id+"F6.imprint","IMPRINT",EDGE,{"disambiguationData":[TD([[subQ2,-1.0]])],"derivedFrom":subQ1}),-1.0]])]});}
            var Q8;
            {var subQ0=sQuery(id+"F6.wireOp",EDGE,"E7.9.7.2");var subQ1=sQuery(id+"F6.wireOp",EDGE,"E7.9.7.1");var subQ2=makeQuery(id+"F6.imprint","INTERSECT",VERTEX,{"derivedFrom":[subQ1,subQ0]});Q8=makeQuery(id+"F6.imprint","IMPRINT",FACE,{"disambiguationData":[TD([[makeQuery(id+"F6.imprint","IMPRINT",EDGE,{"disambiguationData":[TD([[subQ2,-1.0]])],"derivedFrom":subQ1}),-1.0]])]});}
            var Q9;
            {var subQ0=sQuery(id+"F6.wireOp",EDGE,"E7.9.8.2");var subQ1=sQuery(id+"F6.wireOp",EDGE,"E7.9.8.1");var subQ2=makeQuery(id+"F6.imprint","INTERSECT",VERTEX,{"derivedFrom":[subQ1,subQ0]});Q9=makeQuery(id+"F6.imprint","IMPRINT",FACE,{"disambiguationData":[TD([[makeQuery(id+"F6.imprint","IMPRINT",EDGE,{"disambiguationData":[TD([[subQ2,-1.0]])],"derivedFrom":subQ1}),-1.0]])]});}
            var Q10;
            {var subQ0=sQuery(id+"F6.wireOp",EDGE,"E7.9.9.2");var subQ1=sQuery(id+"F6.wireOp",EDGE,"E7.9.9.1");var subQ2=makeQuery(id+"F6.imprint","INTERSECT",VERTEX,{"derivedFrom":[subQ1,subQ0]});Q10=makeQuery(id+"F6.imprint","IMPRINT",FACE,{"disambiguationData":[TD([[makeQuery(id+"F6.imprint","IMPRINT",EDGE,{"disambiguationData":[TD([[subQ2,-1.0]])],"derivedFrom":subQ1}),-1.0]])]});}
            var Q11;
            {var subQ0=sQuery(id+"F6.wireOp",EDGE,"E7.8.9.2");var subQ1=sQuery(id+"F6.wireOp",EDGE,"E7.8.9.1");var subQ2=makeQuery(id+"F6.imprint","INTERSECT",VERTEX,{"derivedFrom":[subQ1,subQ0]});Q11=makeQuery(id+"F6.imprint","IMPRINT",FACE,{"disambiguationData":[TD([[makeQuery(id+"F6.imprint","IMPRINT",EDGE,{"disambiguationData":[TD([[subQ2,-1.0]])],"derivedFrom":subQ1}),-1.0]])]});}
            var Q12;
            {var subQ0=sQuery(id+"F6.wireOp",EDGE,"E7.7.9.2");var subQ1=sQuery(id+"F6.wireOp",EDGE,"E7.7.9.1");var subQ2=makeQuery(id+"F6.imprint","INTERSECT",VERTEX,{"derivedFrom":[subQ1,subQ0]});Q12=makeQuery(id+"F6.imprint","IMPRINT",FACE,{"disambiguationData":[TD([[makeQuery(id+"F6.imprint","IMPRINT",EDGE,{"disambiguationData":[TD([[subQ2,-1.0]])],"derivedFrom":subQ1}),-1.0]])]});}
            var Q13;
            {var subQ0=sQuery(id+"F6.wireOp",EDGE,"E7.6.9.2");var subQ1=sQuery(id+"F6.wireOp",EDGE,"E7.6.9.1");var subQ2=makeQuery(id+"F6.imprint","INTERSECT",VERTEX,{"derivedFrom":[subQ1,subQ0]});Q13=makeQuery(id+"F6.imprint","IMPRINT",FACE,{"disambiguationData":[TD([[makeQuery(id+"F6.imprint","IMPRINT",EDGE,{"disambiguationData":[TD([[subQ2,-1.0]])],"derivedFrom":subQ1}),-1.0]])]});}
            var Q14;
            {var subQ0=sQuery(id+"F6.wireOp",EDGE,"E7.5.9.2");var subQ1=sQuery(id+"F6.wireOp",EDGE,"E7.5.9.1");var subQ2=makeQuery(id+"F6.imprint","INTERSECT",VERTEX,{"derivedFrom":[subQ1,subQ0]});Q14=makeQuery(id+"F6.imprint","IMPRINT",FACE,{"disambiguationData":[TD([[makeQuery(id+"F6.imprint","IMPRINT",EDGE,{"disambiguationData":[TD([[subQ2,-1.0]])],"derivedFrom":subQ1}),-1.0]])]});}
            var Q15;
            {var subQ0=sQuery(id+"F6.wireOp",EDGE,"E7.0.9.1");Q15=makeQuery(id+"F6.imprint","IMPRINT",FACE,{"disambiguationData":[TD([[makeQuery(id+"F6.imprint","IMPRINT",EDGE,{"derivedFrom":subQ0}),-1.0]])]});}
            var Q16;
            {var subQ0=sQuery(id+"F6.wireOp",EDGE,"E7.1.9.2");var subQ1=sQuery(id+"F6.wireOp",EDGE,"E7.1.9.1");var subQ2=makeQuery(id+"F6.imprint","INTERSECT",VERTEX,{"derivedFrom":[subQ1,subQ0]});Q16=makeQuery(id+"F6.imprint","IMPRINT",FACE,{"disambiguationData":[TD([[makeQuery(id+"F6.imprint","IMPRINT",EDGE,{"disambiguationData":[TD([[subQ2,-1.0]])],"derivedFrom":subQ1}),-1.0]])]});}
            var Q17;
            {var subQ0=sQuery(id+"F6.wireOp",EDGE,"E7.2.9.2");var subQ1=sQuery(id+"F6.wireOp",EDGE,"E7.2.9.1");var subQ2=makeQuery(id+"F6.imprint","INTERSECT",VERTEX,{"derivedFrom":[subQ1,subQ0]});Q17=makeQuery(id+"F6.imprint","IMPRINT",FACE,{"disambiguationData":[TD([[makeQuery(id+"F6.imprint","IMPRINT",EDGE,{"disambiguationData":[TD([[subQ2,-1.0]])],"derivedFrom":subQ1}),-1.0]])]});}
            var Q18;
            {var subQ0=sQuery(id+"F6.wireOp",EDGE,"E7.3.9.2");var subQ1=sQuery(id+"F6.wireOp",EDGE,"E7.3.9.1");var subQ2=makeQuery(id+"F6.imprint","INTERSECT",VERTEX,{"derivedFrom":[subQ1,subQ0]});Q18=makeQuery(id+"F6.imprint","IMPRINT",FACE,{"disambiguationData":[TD([[makeQuery(id+"F6.imprint","IMPRINT",EDGE,{"disambiguationData":[TD([[subQ2,-1.0]])],"derivedFrom":subQ1}),-1.0]])]});}
            var Q19;
            {var subQ0=sQuery(id+"F6.wireOp",EDGE,"E7.4.9.2");var subQ1=sQuery(id+"F6.wireOp",EDGE,"E7.4.9.1");var subQ2=makeQuery(id+"F6.imprint","INTERSECT",VERTEX,{"derivedFrom":[subQ1,subQ0]});Q19=makeQuery(id+"F6.imprint","IMPRINT",FACE,{"disambiguationData":[TD([[makeQuery(id+"F6.imprint","IMPRINT",EDGE,{"disambiguationData":[TD([[subQ2,-1.0]])],"derivedFrom":subQ1}),-1.0]])]});}
            extrude(context, id + "F7", {"entities" : qUnion([Q0, Q1, Q2, Q3, Q4, Q5, Q6, Q7, Q8, Q9, Q10, Q11, Q12, Q13, Q14, Q15, Q16, Q17, Q18, Q19]), "operationType" : NewBodyOperationType.REMOVE, "endBound" : BoundingType.THROUGH_ALL, "oppositeDirection" : true, "depth" : 25 * mm});
        }
        {
            var Q0;
            {var subQ0=sQuery(id+"F0.wireOp",EDGE,"E0.right");var subQ1=sQuery(id+"F0.wireOp",EDGE,"E0.top");var subQ2=sQuery(id+"F0.wireOp",EDGE,"E0.bottom");Q0=makeQuery(id+"F3.boolean.opBoolean","SPLIT",FACE,{"disambiguationData":[TD([makeQuery(id+"F1.opExtrude","SWEPT_FACE",FACE,{"disambiguationData":[OSD([subQ0])]})])],"derivedFrom":makeQuery(id+"F1.opExtrude","CAP_FACE",FACE,{"disambiguationData":[OSD([subQ2,subQ1,sQuery(id+"F0.wireOp",EDGE,"E0.left"),subQ0])],"isStart":false})});}
            var sketch = newSketch(context, id + "F8", { "sketchPlane" : qUnion([Q0])});
            skLineSegment(sketch, "E8", {"start": v(-8, 1.5) * mm, "end": v(-7.46, -1.5) * mm});
            skSolve(sketch);
        }
        {
            var Q0;
            {var subQ0=sQuery(id+"F8.wireOp",EDGE,"E8");Q0=makeQuery(id+"F8.imprint","IMPRINT",FACE,{"disambiguationData":[TD([[makeQuery(id+"F8.imprint","IMPRINT",EDGE,{"derivedFrom":subQ0}),-1.0]])]});}
            extrude(context, id + "F9", {"entities" : qUnion([Q0]), "operationType" : NewBodyOperationType.REMOVE, "endBound" : BoundingType.THROUGH_ALL, "oppositeDirection" : true, "depth" : 25 * mm});
        }
    });
